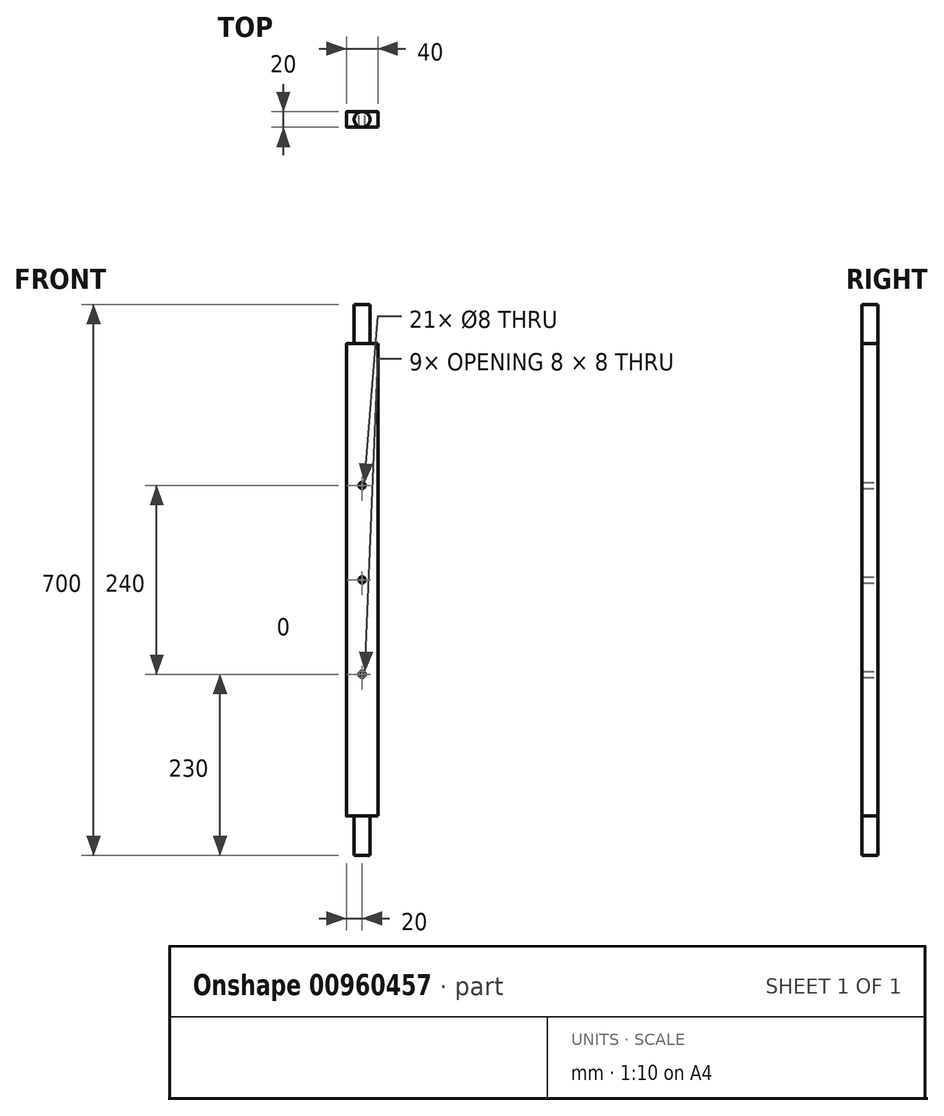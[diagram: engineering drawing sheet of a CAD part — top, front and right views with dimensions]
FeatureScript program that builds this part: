
annotation { "Feature Type Name" : "Feature", "Feature Type Description" : "" }
export const myFeature = defineFeature(function(context is Context, id is Id, definition is map)
    precondition{}
    {
        {
            var Q0;
            Q0=qCreatedBy(makeId("Front.planeOp"),FACE);
            var sketch = newSketch(context, id + "F0", { "sketchPlane" : qUnion([Q0])});
            skLineSegment(sketch, "E0.bottom", {"start": v(0, 0) * mm, "end": v(40, 0) * mm});
            skLineSegment(sketch, "E0.top", {"start": v(0, 700) * mm, "end": v(40, 700) * mm});
            skLineSegment(sketch, "E0.left", {"start": v(0, 0) * mm, "end": v(0, 700) * mm});
            skLineSegment(sketch, "E0.right", {"start": v(40, 0) * mm, "end": v(40, 700) * mm});
            skSolve(sketch);
        }
        {
            var Q0;
            Q0=makeQuery(id+"F0.imprint","IMPRINT",FACE,{"disambiguationData":[TD([[makeQuery(id+"F0.imprint","IMPRINT",EDGE,{"derivedFrom":sQuery(id+"F0.wireOp",EDGE,"E0.bottom")}),1.0]])]});
            extrude(context, id + "F1", {"entities" : qUnion([Q0]), "depth" : 20 * mm, "offsetDistance" : 25 * mm});
        }
        {
            var Q0;
            Q0=makeQuery(id+"F1.opExtrude","SWEPT_FACE",FACE,{"disambiguationData":[OSD([sQuery(id+"F0.wireOp",EDGE,"E0.top")])]});
            var sketch = newSketch(context, id + "F2", { "sketchPlane" : qUnion([Q0])});
            skCircle(sketch, "E1", {"center": v(20, -10) * mm, "radius": 10 * mm});
            skPoint(sketch, "E1.centerSnap0", {"position": v(40, -10) * mm});
            skPoint(sketch, "E1.centerSnap1", {"position": v(20, 0) * mm});
            skSolve(sketch);
        }
        {
            var Q0;
            {var subQ1=sQuery(id+"F0.wireOp",EDGE,"E0.top");var subQ6=makeQuery(id+"F1.opExtrude","SWEPT_EDGE",EDGE,{"disambiguationData":[OSD([subQ1,sQuery(id+"F0.wireOp",EDGE,"E0.right")])]});Q0=makeQuery(id+"F2.imprint","IMPRINT",FACE,{"disambiguationData":[TD([[makeQuery(id+"F2.imprint","IMPRINT",EDGE,{"derivedFrom":subQ6}),1.0]])]});}
            var Q1;
            {var subQ1=sQuery(id+"F0.wireOp",EDGE,"E0.top");var subQ6=makeQuery(id+"F1.opExtrude","SWEPT_EDGE",EDGE,{"disambiguationData":[OSD([subQ1,sQuery(id+"F0.wireOp",EDGE,"E0.left")])]});Q1=makeQuery(id+"F2.imprint","IMPRINT",FACE,{"disambiguationData":[TD([[makeQuery(id+"F2.imprint","IMPRINT",EDGE,{"derivedFrom":subQ6}),-1.0]])]});}
            extrude(context, id + "F3", {"entities" : qUnion([Q0, Q1]), "operationType" : NewBodyOperationType.REMOVE, "oppositeDirection" : true, "depth" : 50 * mm, "offsetDistance" : 25 * mm});
        }
        {
            var Q0;
            Q0=makeQuery(id+"F1.opExtrude","SWEPT_FACE",FACE,{"disambiguationData":[OSD([sQuery(id+"F0.wireOp",EDGE,"E0.bottom")])]});
            var sketch = newSketch(context, id + "F4", { "sketchPlane" : qUnion([Q0])});
            skCircle(sketch, "E2", {"center": v(20, 10) * mm, "radius": 10 * mm});
            skPoint(sketch, "E2.centerSnap0", {"position": v(0, 10) * mm});
            skPoint(sketch, "E2.centerSnap1", {"position": v(20, 0) * mm});
            skSolve(sketch);
        }
        {
            var Q0;
            {var subQ1=sQuery(id+"F0.wireOp",EDGE,"E0.bottom");var subQ6=makeQuery(id+"F1.opExtrude","SWEPT_EDGE",EDGE,{"disambiguationData":[OSD([subQ1,sQuery(id+"F0.wireOp",EDGE,"E0.left")])]});Q0=makeQuery(id+"F4.imprint","IMPRINT",FACE,{"disambiguationData":[TD([[makeQuery(id+"F4.imprint","IMPRINT",EDGE,{"derivedFrom":subQ6}),1.0]])]});}
            var Q1;
            {var subQ1=sQuery(id+"F0.wireOp",EDGE,"E0.bottom");var subQ6=makeQuery(id+"F1.opExtrude","SWEPT_EDGE",EDGE,{"disambiguationData":[OSD([subQ1,sQuery(id+"F0.wireOp",EDGE,"E0.right")])]});Q1=makeQuery(id+"F4.imprint","IMPRINT",FACE,{"disambiguationData":[TD([[makeQuery(id+"F4.imprint","IMPRINT",EDGE,{"derivedFrom":subQ6}),-1.0]])]});}
            extrude(context, id + "F5", {"entities" : qUnion([Q0, Q1]), "operationType" : NewBodyOperationType.REMOVE, "oppositeDirection" : true, "depth" : 50 * mm, "offsetDistance" : 25 * mm});
        }
        {
            var Q0;
            Q0=makeQuery(id+"F1.opExtrude","CAP_FACE",FACE,{"disambiguationData":[OSD([sQuery(id+"F0.wireOp",EDGE,"E0.bottom"),sQuery(id+"F0.wireOp",EDGE,"E0.top"),sQuery(id+"F0.wireOp",EDGE,"E0.left"),sQuery(id+"F0.wireOp",EDGE,"E0.right")])],"isStart":true});
            var sketch = newSketch(context, id + "F6", { "sketchPlane" : qUnion([Q0])});
            skCircle(sketch, "E3", {"center": v(-20, 470) * mm, "radius": 4 * mm});
            skCircle(sketch, "E4", {"center": v(-20, 230) * mm, "radius": 4 * mm});
            skCircle(sketch, "E5", {"center": v(-20, 350) * mm, "radius": 4 * mm});
            skSolve(sketch);
        }
        {
            var Q0;
            Q0=makeQuery(id+"F6.imprint","IMPRINT",FACE,{"disambiguationData":[TD([[makeQuery(id+"F6.imprint","IMPRINT",EDGE,{"derivedFrom":sQuery(id+"F6.wireOp",EDGE,"E3")}),1.0]])]});
            var Q1;
            Q1=makeQuery(id+"F6.imprint","IMPRINT",FACE,{"disambiguationData":[TD([[makeQuery(id+"F6.imprint","IMPRINT",EDGE,{"derivedFrom":sQuery(id+"F6.wireOp",EDGE,"E4")}),1.0]])]});
            var Q2;
            Q2=makeQuery(id+"F6.imprint","IMPRINT",FACE,{"disambiguationData":[TD([[makeQuery(id+"F6.imprint","IMPRINT",EDGE,{"derivedFrom":sQuery(id+"F6.wireOp",EDGE,"E5")}),1.0]])]});
            extrude(context, id + "F7", {"entities" : qUnion([Q0, Q1, Q2]), "operationType" : NewBodyOperationType.REMOVE, "oppositeDirection" : true, "depth" : 25 * mm, "offsetDistance" : 25 * mm});
        }
        {
            var Q0;
            Q0=makeQuery(id+"F1.opExtrude","CAP_EDGE",EDGE,{"disambiguationData":[OSD([sQuery(id+"F0.wireOp",EDGE,"E0.left")])],"isStart":true});
            var Q1;
            Q1=makeQuery(id+"F1.opExtrude","CAP_EDGE",EDGE,{"disambiguationData":[OSD([sQuery(id+"F0.wireOp",EDGE,"E0.left")])],"isStart":false});
            var Q2;
            Q2=makeQuery(id+"F1.opExtrude","CAP_EDGE",EDGE,{"disambiguationData":[OSD([sQuery(id+"F0.wireOp",EDGE,"E0.right")])],"isStart":true});
            var Q3;
            Q3=makeQuery(id+"F1.opExtrude","CAP_EDGE",EDGE,{"disambiguationData":[OSD([sQuery(id+"F0.wireOp",EDGE,"E0.right")])],"isStart":false});
            fillet(context, id + "F8", {"entities" : qUnion([Q0, Q1, Q2, Q3]), "radius" : .5 * mm, "tangentPropagation" : true, "allowEdgeOverflow" : false});
        }
    });
